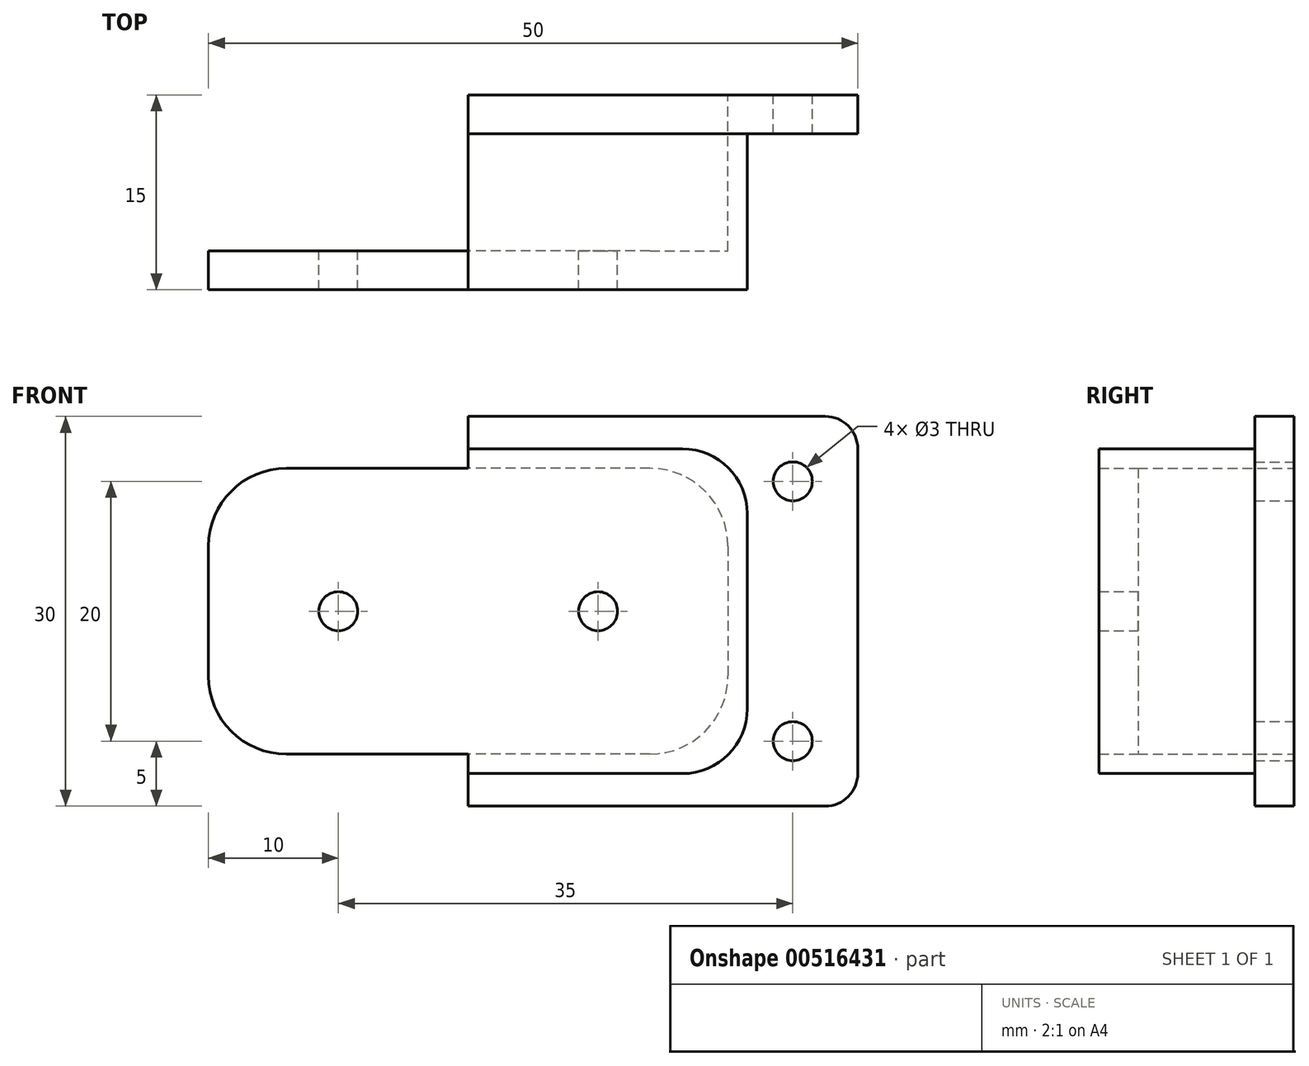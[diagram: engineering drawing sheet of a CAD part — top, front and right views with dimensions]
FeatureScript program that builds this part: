
annotation { "Feature Type Name" : "Feature", "Feature Type Description" : "" }
export const myFeature = defineFeature(function(context is Context, id is Id, definition is map)
    precondition{}
    {
        {
            var Q0;
            Q0=qCreatedBy(makeId("Front.planeOp"),FACE);
            var sketch = newSketch(context, id + "F0", { "sketchPlane" : qUnion([Q0])});
            skLineSegment(sketch, "E0.bottom", {"start": v(0, 15) * mm, "end": v(27.5, 15) * mm});
            skLineSegment(sketch, "E0.top", {"start": v(0, -15) * mm, "end": v(27.5, -15) * mm});
            skLineSegment(sketch, "E0.left", {"start": v(0, 15) * mm, "end": v(0, -15) * mm});
            skLineSegment(sketch, "E0.right", {"start": v(30, 12.5) * mm, "end": v(30, -12.5) * mm});
            skPoint(sketch, "E1.visualSharp", {"position": v(0, 15) * mm});
            skPoint(sketch, "E2.visualSharp", {"position": v(0, -15) * mm});
            skPoint(sketch, "E3.visualSharp", {"position": v(30, -15) * mm});
            skArc(sketch, "E3.filletArc", {"start": v(27.5, -15) * mm, "mid": v(29.27, -14.27) * mm, "end": v(30, -12.5) * mm});
            skPoint(sketch, "E4.visualSharp", {"position": v(30, 15) * mm});
            skArc(sketch, "E4.filletArc", {"start": v(30, 12.5) * mm, "mid": v(29.27, 14.27) * mm, "end": v(27.5, 15) * mm});
            skLineSegment(sketch, "E5.bottom", {"start": v(0, 11) * mm, "end": v(14, 11) * mm});
            skLineSegment(sketch, "E5.top", {"start": v(0, -11) * mm, "end": v(14, -11) * mm});
            skLineSegment(sketch, "E5.left", {"start": v(0, 11) * mm, "end": v(0, -11) * mm});
            skLineSegment(sketch, "E5.right", {"start": v(20, 5) * mm, "end": v(20, -5) * mm});
            skCircle(sketch, "E6", {"center": v(25, 10) * mm, "radius": 1.5 * mm});
            skCircle(sketch, "E7", {"center": v(25, -10) * mm, "radius": 1.5 * mm});
            skCircle(sketch, "E8", {"center": v(10, 0) * mm, "radius": 1.5 * mm});
            skArc(sketch, "E9.MirrorCS", {"start": v(-27.5, -15) * mm, "mid": v(-29.27, -14.27) * mm, "end": v(-30, -12.5) * mm});
            skArc(sketch, "E10.MirrorCS", {"start": v(-30, 12.5) * mm, "mid": v(-29.27, 14.27) * mm, "end": v(-27.5, 15) * mm});
            skPoint(sketch, "E11.MirrorP", {"position": v(-30, -15) * mm});
            skLineSegment(sketch, "E12.MirrorCS", {"start": v(0, 15) * mm, "end": v(-27.5, 15) * mm});
            skLineSegment(sketch, "E13.MirrorCS", {"start": v(0, -15) * mm, "end": v(-27.5, -15) * mm});
            skLineSegment(sketch, "E14.MirrorCS", {"start": v(-30, 12.5) * mm, "end": v(-30, -12.5) * mm});
            skLineSegment(sketch, "E15.MirrorCS", {"start": v(0, -11) * mm, "end": v(-14, -11) * mm});
            skPoint(sketch, "E16.MirrorP", {"position": v(-30, 15) * mm});
            skCircle(sketch, "E17.MirrorC", {"center": v(-10, 0) * mm, "radius": 1.5 * mm});
            skLineSegment(sketch, "E18.MirrorCS", {"start": v(0, 11) * mm, "end": v(-14, 11) * mm});
            skCircle(sketch, "E19.MirrorC", {"center": v(-25, -10) * mm, "radius": 1.5 * mm});
            skCircle(sketch, "E20.MirrorC", {"center": v(-25, 10) * mm, "radius": 1.5 * mm});
            skLineSegment(sketch, "E21.MirrorCS", {"start": v(-20, 5) * mm, "end": v(-20, -5) * mm});
            skPoint(sketch, "E22.visualSharp", {"position": v(20, 11) * mm});
            skArc(sketch, "E22.filletArc", {"start": v(20, 5) * mm, "mid": v(18.24, 9.24) * mm, "end": v(14, 11) * mm});
            skPoint(sketch, "E23.visualSharp", {"position": v(20, -11) * mm});
            skArc(sketch, "E23.filletArc", {"start": v(14, -11) * mm, "mid": v(18.24, -9.24) * mm, "end": v(20, -5) * mm});
            skPoint(sketch, "E24.visualSharp", {"position": v(-20, 11) * mm});
            skArc(sketch, "E24.filletArc", {"start": v(-14, 11) * mm, "mid": v(-18.24, 9.24) * mm, "end": v(-20, 5) * mm});
            skPoint(sketch, "E25.visualSharp", {"position": v(-20, -11) * mm});
            skArc(sketch, "E25.filletArc", {"start": v(-20, -5) * mm, "mid": v(-18.24, -9.24) * mm, "end": v(-14, -11) * mm});
            skSolve(sketch);
        }
        {
            var Q0;
            Q0=makeQuery(id+"F0.imprint","IMPRINT",FACE,{"disambiguationData":[TD([[makeQuery(id+"F0.imprint","IMPRINT",EDGE,{"derivedFrom":sQuery(id+"F0.wireOp",EDGE,"E9.MirrorCS")}),-1.0]])]});
            var Q1;
            {var subQ1=sQuery(id+"F0.wireOp",EDGE,"E15.MirrorCS");Q1=makeQuery(id+"F0.imprint","IMPRINT",FACE,{"disambiguationData":[TD([[makeQuery(id+"F0.imprint","IMPRINT",EDGE,{"derivedFrom":subQ1}),-1.0]])]});}
            var Q2;
            {var subQ1=sQuery(id+"F0.wireOp",EDGE,"E5.bottom");Q2=makeQuery(id+"F0.imprint","IMPRINT",FACE,{"disambiguationData":[TD([[makeQuery(id+"F0.imprint","IMPRINT",EDGE,{"derivedFrom":subQ1}),-1.0]])]});}
            var Q3;
            {var subQ2=sQuery(id+"F0.wireOp",EDGE,"E0.bottom");Q3=makeQuery(id+"F0.imprint","IMPRINT",FACE,{"disambiguationData":[TD([[makeQuery(id+"F0.imprint","IMPRINT",EDGE,{"derivedFrom":subQ2}),-1.0]])]});}
            extrude(context, id + "F1", {"entities" : qUnion([Q0, Q1, Q2, Q3]), "depth" : 15 * mm, "offsetDistance" : 25 * mm});
        }
        {
            var Q0;
            {var subQ1=sQuery(id+"F0.wireOp",EDGE,"E15.MirrorCS");Q0=makeQuery(id+"F0.imprint","IMPRINT",FACE,{"disambiguationData":[TD([[makeQuery(id+"F0.imprint","IMPRINT",EDGE,{"derivedFrom":subQ1}),-1.0]])]});}
            var Q1;
            {var subQ1=sQuery(id+"F0.wireOp",EDGE,"E5.bottom");Q1=makeQuery(id+"F0.imprint","IMPRINT",FACE,{"disambiguationData":[TD([[makeQuery(id+"F0.imprint","IMPRINT",EDGE,{"derivedFrom":subQ1}),-1.0]])]});}
            extrude(context, id + "F2", {"entities" : qUnion([Q0, Q1]), "operationType" : NewBodyOperationType.REMOVE, "depth" : 12 * mm, "offsetDistance" : 25 * mm});
        }
        {
            var Q0;
            Q0=makeQuery(id+"F1.opExtrude","CAP_FACE",FACE,{"disambiguationData":[OSD([sQuery(id+"F0.wireOp",EDGE,"E0.bottom"),sQuery(id+"F0.wireOp",EDGE,"E0.top"),sQuery(id+"F0.wireOp",EDGE,"E0.right"),sQuery(id+"F0.wireOp",EDGE,"E3.filletArc"),sQuery(id+"F0.wireOp",EDGE,"E4.filletArc"),sQuery(id+"F0.wireOp",EDGE,"E6"),sQuery(id+"F0.wireOp",EDGE,"E7"),sQuery(id+"F0.wireOp",EDGE,"E8"),sQuery(id+"F0.wireOp",EDGE,"E9.MirrorCS"),sQuery(id+"F0.wireOp",EDGE,"E10.MirrorCS"),sQuery(id+"F0.wireOp",EDGE,"E12.MirrorCS"),sQuery(id+"F0.wireOp",EDGE,"E13.MirrorCS"),sQuery(id+"F0.wireOp",EDGE,"E14.MirrorCS"),sQuery(id+"F0.wireOp",EDGE,"E17.MirrorC"),sQuery(id+"F0.wireOp",EDGE,"E19.MirrorC"),sQuery(id+"F0.wireOp",EDGE,"E20.MirrorC")])],"isStart":false});
            var sketch = newSketch(context, id + "F3", { "sketchPlane" : qUnion([Q0])});
            skLineSegment(sketch, "E26.bottom", {"start": v(-16.5, 12.5) * mm, "end": v(16.5, 12.5) * mm});
            skLineSegment(sketch, "E26.top", {"start": v(-16.5, -12.5) * mm, "end": v(16.5, -12.5) * mm});
            skLineSegment(sketch, "E26.left", {"start": v(-21.5, 7.5) * mm, "end": v(-21.5, -7.5) * mm});
            skLineSegment(sketch, "E26.right", {"start": v(21.5, 7.5) * mm, "end": v(21.5, -7.5) * mm});
            skPoint(sketch, "E27.visualSharp", {"position": v(-21.5, 12.5) * mm});
            skArc(sketch, "E27.filletArc", {"start": v(-16.5, 12.5) * mm, "mid": v(-20.04, 11.04) * mm, "end": v(-21.5, 7.5) * mm});
            skPoint(sketch, "E28.visualSharp", {"position": v(-21.5, -12.5) * mm});
            skArc(sketch, "E28.filletArc", {"start": v(-21.5, -7.5) * mm, "mid": v(-20.04, -11.04) * mm, "end": v(-16.5, -12.5) * mm});
            skPoint(sketch, "E29.visualSharp", {"position": v(21.5, 12.5) * mm});
            skArc(sketch, "E29.filletArc", {"start": v(21.5, 7.5) * mm, "mid": v(20.04, 11.04) * mm, "end": v(16.5, 12.5) * mm});
            skPoint(sketch, "E30.visualSharp", {"position": v(21.5, -12.5) * mm});
            skArc(sketch, "E30.filletArc", {"start": v(16.5, -12.5) * mm, "mid": v(20.04, -11.04) * mm, "end": v(21.5, -7.5) * mm});
            skSolve(sketch);
        }
        {
            var Q0;
            Q0=makeQuery(id+"F3.imprint","IMPRINT",FACE,{"disambiguationData":[TD([[makeQuery(id+"F3.imprint","IMPRINT",EDGE,{"derivedFrom":sQuery(id+"F3.wireOp",EDGE,"E26.bottom")}),1.0]])]});
            extrude(context, id + "F4", {"entities" : qUnion([Q0]), "operationType" : NewBodyOperationType.REMOVE, "oppositeDirection" : true, "depth" : 12 * mm, "offsetDistance" : 25 * mm});
        }
    });
